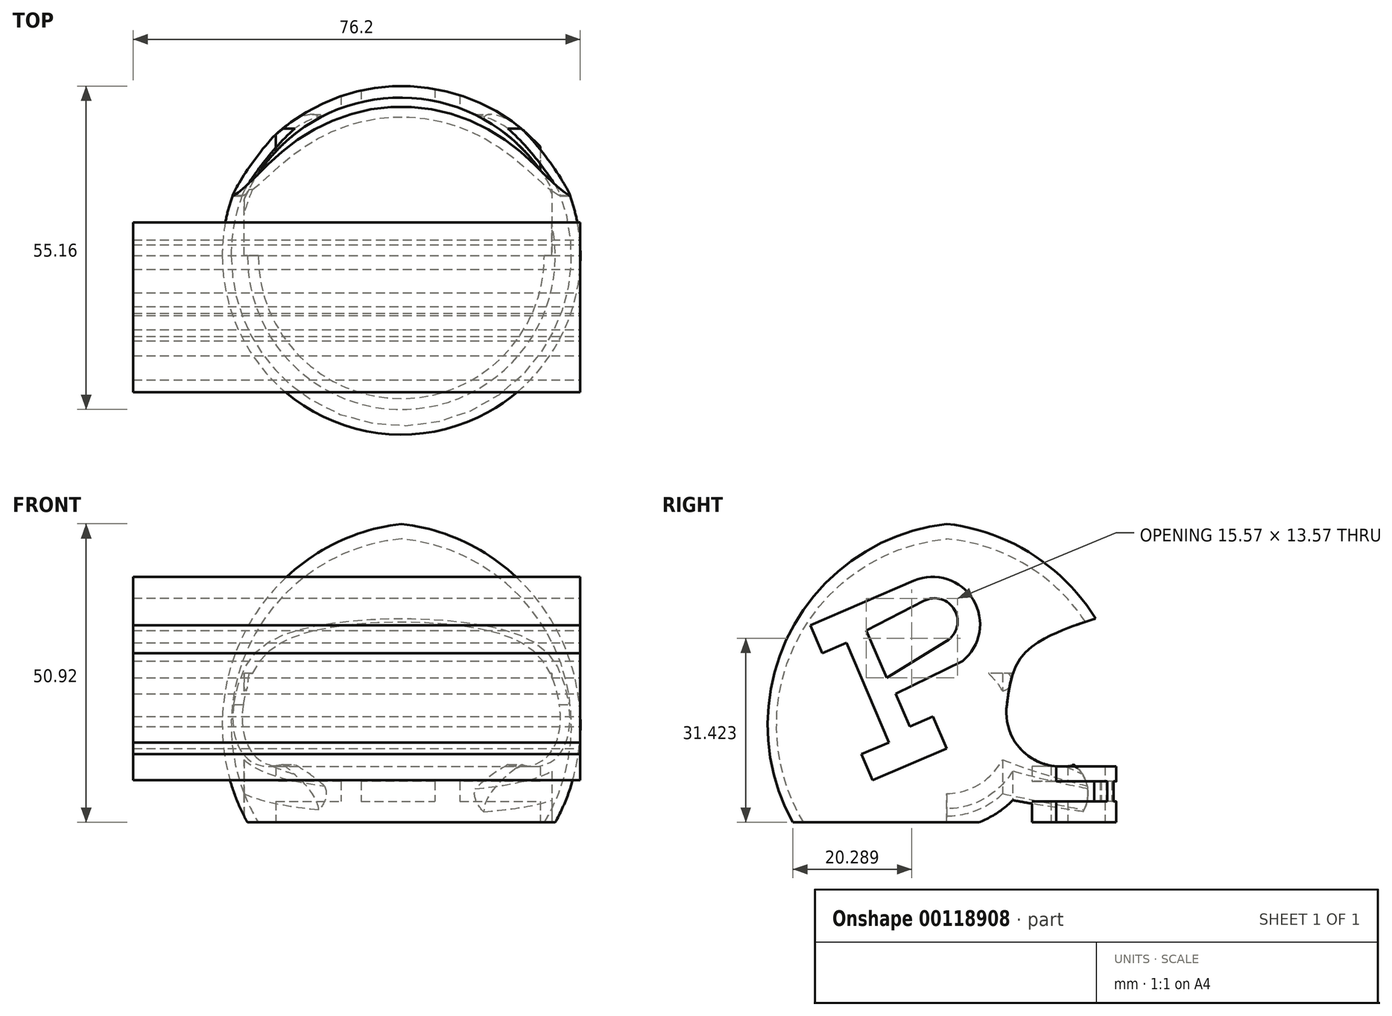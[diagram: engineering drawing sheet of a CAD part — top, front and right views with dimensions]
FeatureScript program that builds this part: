
annotation { "Feature Type Name" : "Feature", "Feature Type Description" : "" }
export const myFeature = defineFeature(function(context is Context, id is Id, definition is map)
    precondition{}
    {
        {
            var Q0;
            Q0=qCreatedBy(makeId("Front.planeOp"),FACE);
            var sketch = newSketch(context, id + "F0", { "sketchPlane" : qUnion([Q0])});
            skArc(sketch, "E0", {"start": v(26.24, 0) * mm, "mid": v(26.7, 32.45) * mm, "end": v(0, 50.92) * mm});
            skLineSegment(sketch, "E1", {"start": v(0, 50.92) * mm, "end": v(0, 0) * mm});
            skLineSegment(sketch, "E2", {"start": v(0, 0) * mm, "end": v(22.53, 0) * mm});
            skLineSegment(sketch, "E3", {"start": v(22.53, 0) * mm, "end": v(26.24, 0) * mm});
            skArc(sketch, "E4", {"start": v(24.39, 0) * mm, "mid": v(25.58, 30.92) * mm, "end": v(0, 48.35) * mm});
            skSolve(sketch);
        }
        {
            var Q0;
            {var subQ0=sQuery(id+"F0.wireOp",EDGE,"E0");Q0=makeQuery(id+"F0.imprint","IMPRINT",FACE,{"disambiguationData":[TD([[makeQuery(id+"F0.imprint","IMPRINT",EDGE,{"derivedFrom":subQ0}),1.0]])]});}
            var Q1;
            Q1=sQuery(id+"F0.wireOp",EDGE,"E1");
            revolve(context, id + "F1", {"entities" : qUnion([Q0]), "axis" : qUnion([Q1]), "revolveType" : RevolveType.FULL});
        }
        {
            var Q0;
            Q0=qCreatedBy(makeId("Right.planeOp"),FACE);
            cPlane(context, id + "F2", {"entities" : qUnion([Q0]), "cplaneType" : CPlaneType.OFFSET, "offset" : 30.48 * mm, "width" : 152.4 * mm, "height" : 152.4 * mm});
        }
        {
            var Q0;
            Q0=qCreatedBy(id+"F2.planeOp",FACE);
            var sketch = newSketch(context, id + "F3", { "sketchPlane" : qUnion([Q0])});
            skArc(sketch, "E5", {"start": v(10.27, 20.1) * mm, "mid": v(13.21, 11.9) * mm, "end": v(21.68, 9.84) * mm});
            skFitSpline(sketch, "E6", {"points": [v(10.27, 20.1) * mm, v(13.12, 28.67) * mm, v(26.81, 35.23) * mm], "startDerivative": vector(2.7, 21.4) * mm, "endDerivative": vector(29.24, 9.35) * mm});
            skLineSegment(sketch, "E7", {"start": v(36.51, 0) * mm, "end": v(36.51, 35.23) * mm});
            skLineSegment(sketch, "E8", {"start": v(26.81, 35.23) * mm, "end": v(36.51, 35.23) * mm});
            skLineSegment(sketch, "E9", {"start": v(36.51, 0) * mm, "end": v(21.68, 0) * mm});
            skArc(sketch, "E10", {"start": v(21.68, 0) * mm, "mid": v(24.08, 4.92) * mm, "end": v(21.68, 9.84) * mm});
            skSolve(sketch);
        }
        {
            var Q0;
            {var subQ1=sQuery(id+"F3.wireOp",EDGE,"E5");Q0=makeQuery(id+"F3.imprint","IMPRINT",FACE,{"disambiguationData":[TD([[makeQuery(id+"F3.imprint","IMPRINT",EDGE,{"derivedFrom":subQ1}),1.0]])]});}
            extrude(context, id + "F4", {"entities" : qUnion([Q0]), "operationType" : NewBodyOperationType.REMOVE, "oppositeDirection" : true, "depth" : 101.6 * mm});
        }
        {
            var Q0;
            Q0=qCreatedBy(makeId("Front.planeOp"),FACE);
            var sketch = newSketch(context, id + "F5", { "sketchPlane" : qUnion([Q0])});
            skLineSegment(sketch, "E11", {"start": v(23.67, 9.56) * mm, "end": v(23.67, 6.99) * mm});
            skLineSegment(sketch, "E12", {"start": v(23.67, 6.99) * mm, "end": v(-21.4, 6.99) * mm});
            skLineSegment(sketch, "E13", {"start": v(-21.4, 6.99) * mm, "end": v(-21.4, 9.56) * mm});
            skLineSegment(sketch, "E14", {"start": v(-21.4, 9.56) * mm, "end": v(23.67, 9.56) * mm});
            skLineSegment(sketch, "E15", {"start": v(9.98, 6.99) * mm, "end": v(9.98, 3.57) * mm});
            skLineSegment(sketch, "E16", {"start": v(9.98, 3.57) * mm, "end": v(5.7, 3.57) * mm});
            skLineSegment(sketch, "E17", {"start": v(5.7, 3.57) * mm, "end": v(5.7, 6.99) * mm});
            skLineSegment(sketch, "E18", {"start": v(5.7, 6.99) * mm, "end": v(9.98, 6.99) * mm});
            skLineSegment(sketch, "E19", {"start": v(-6.85, 6.99) * mm, "end": v(-6.85, 3.57) * mm});
            skLineSegment(sketch, "E20", {"start": v(-6.85, 3.57) * mm, "end": v(-10.27, 3.57) * mm});
            skLineSegment(sketch, "E21", {"start": v(-10.27, 3.57) * mm, "end": v(-10.27, 6.99) * mm});
            skLineSegment(sketch, "E22", {"start": v(-10.27, 6.99) * mm, "end": v(-6.85, 6.99) * mm});
            skLineSegment(sketch, "E23", {"start": v(9.98, 3.57) * mm, "end": v(23.67, 3.57) * mm});
            skLineSegment(sketch, "E24", {"start": v(23.67, 3.57) * mm, "end": v(23.67, 0) * mm});
            skLineSegment(sketch, "E25", {"start": v(23.67, 0) * mm, "end": v(-21.4, 0) * mm});
            skLineSegment(sketch, "E26", {"start": v(-21.4, 0) * mm, "end": v(-21.4, 3.57) * mm});
            skLineSegment(sketch, "E27", {"start": v(-21.4, 3.57) * mm, "end": v(-10.27, 3.57) * mm});
            skLineSegment(sketch, "E28", {"start": v(-6.85, 3.57) * mm, "end": v(5.7, 3.57) * mm});
            skSolve(sketch);
        }
        {
            var Q0;
            Q0 = qSketchRegion(id + "F5", true);
            extrude(context, id + "F6", {"entities" : qUnion([Q0]), "oppositeDirection" : true, "depth" : 50.8 * mm});
        }
        {
            var Q0;
            Q0=qCreatedBy(makeId("Top.planeOp"),FACE);
            var sketch = newSketch(context, id + "F7", { "sketchPlane" : qUnion([Q0])});
            skArc(sketch, "E29", {"start": v(28.8, 11.27) * mm, "mid": v(-0.83, 28.9) * mm, "end": v(-29.38, 9.56) * mm});
            skLineSegment(sketch, "E30", {"start": v(-29.38, 9.56) * mm, "end": v(-26.81, 9.56) * mm});
            skArc(sketch, "E31", {"start": v(25.67, 11.27) * mm, "mid": v(-1.1, 26.95) * mm, "end": v(-26.81, 9.56) * mm});
            skLineSegment(sketch, "E32", {"start": v(25.67, 11.27) * mm, "end": v(28.8, 11.27) * mm});
            skLineSegment(sketch, "E33", {"start": v(-26.81, 9.56) * mm, "end": v(-26.81, 0) * mm});
            skLineSegment(sketch, "E34", {"start": v(-26.81, 0) * mm, "end": v(0, 0) * mm});
            skLineSegment(sketch, "E35", {"start": v(0, 0) * mm, "end": v(25.67, 0) * mm});
            skLineSegment(sketch, "E36", {"start": v(25.67, 0) * mm, "end": v(25.67, 11.27) * mm});
            skLineSegment(sketch, "E37", {"start": v(-29.38, 50.8) * mm, "end": v(-29.38, 9.56) * mm});
            skLineSegment(sketch, "E38", {"start": v(28.8, 50.8) * mm, "end": v(28.8, 11.27) * mm});
            skLineSegment(sketch, "E39", {"start": v(-29.38, 50.8) * mm, "end": v(28.8, 50.8) * mm});
            skSolve(sketch);
        }
        {
            var Q0;
            Q0=makeQuery(id+"F7.imprint","IMPRINT",FACE,{"disambiguationData":[TD([[makeQuery(id+"F7.imprint","IMPRINT",EDGE,{"derivedFrom":sQuery(id+"F7.wireOp",EDGE,"E29")}),-1.0]])]});
            var Q1;
            Q1=makeQuery(id+"F7.imprint","IMPRINT",FACE,{"disambiguationData":[TD([[makeQuery(id+"F7.imprint","IMPRINT",EDGE,{"derivedFrom":sQuery(id+"F7.wireOp",EDGE,"E31")}),1.0]])]});
            extrude(context, id + "F8", {"entities" : qUnion([Q0, Q1]), "operationType" : NewBodyOperationType.REMOVE, "depth" : 25.4 * mm});
        }
        {
            var Q0;
            Q0=qCreatedBy(id+"F2.planeOp",FACE);
            var sketch = newSketch(context, id + "F9", { "sketchPlane" : qUnion([Q0])});
            skArc(sketch, "E40", {"start": v(0, 30.95) * mm, "mid": v(1.36, 36.22) * mm, "end": v(-3.85, 37.8) * mm});
            skArc(sketch, "E41", {"start": v(2.7, 27.53) * mm, "mid": v(4.53, 37.97) * mm, "end": v(-5.56, 41.22) * mm});
            skLineSegment(sketch, "E42", {"start": v(0, 30.95) * mm, "end": v(-10.24, 24.64) * mm});
            skLineSegment(sketch, "E43", {"start": v(-3.85, 37.8) * mm, "end": v(-13.74, 32.74) * mm});
            skLineSegment(sketch, "E44", {"start": v(-13.74, 32.74) * mm, "end": v(-10.24, 24.64) * mm});
            skLineSegment(sketch, "E45", {"start": v(-5.56, 41.22) * mm, "end": v(-23.26, 33.65) * mm});
            skLineSegment(sketch, "E46", {"start": v(-23.26, 33.65) * mm, "end": v(-21.22, 28.88) * mm});
            skLineSegment(sketch, "E47", {"start": v(-21.22, 28.88) * mm, "end": v(-17.1, 30.65) * mm});
            skLineSegment(sketch, "E48", {"start": v(-17.1, 30.65) * mm, "end": v(-9.81, 13.64) * mm});
            skLineSegment(sketch, "E49", {"start": v(-9.81, 13.64) * mm, "end": v(-14.52, 11.63) * mm});
            skLineSegment(sketch, "E50", {"start": v(-14.52, 11.63) * mm, "end": v(-12.62, 7.18) * mm});
            skLineSegment(sketch, "E51", {"start": v(-12.62, 7.18) * mm, "end": v(0, 12.58) * mm});
            skLineSegment(sketch, "E52", {"start": v(0, 12.58) * mm, "end": v(-2.33, 18.03) * mm});
            skLineSegment(sketch, "E53", {"start": v(-2.33, 18.03) * mm, "end": v(-6.3, 16.33) * mm});
            skPoint(sketch, "E53.endSnap0", {"position": v(-6.3, 9.88) * mm});
            skLineSegment(sketch, "E54", {"start": v(-6.3, 16.33) * mm, "end": v(-8.7, 21.94) * mm});
            skLineSegment(sketch, "E55", {"start": v(-8.7, 21.94) * mm, "end": v(2.7, 27.53) * mm});
            skSolve(sketch);
        }
        {
            var Q0;
            Q0=makeQuery(id+"F9.imprint","IMPRINT",FACE,{"disambiguationData":[TD([[makeQuery(id+"F9.imprint","IMPRINT",EDGE,{"derivedFrom":sQuery(id+"F9.wireOp",EDGE,"E40")}),-1.0]])]});
            extrude(context, id + "F10", {"entities" : qUnion([Q0]), "oppositeDirection" : true, "depth" : 76.2 * mm});
        }
    });
